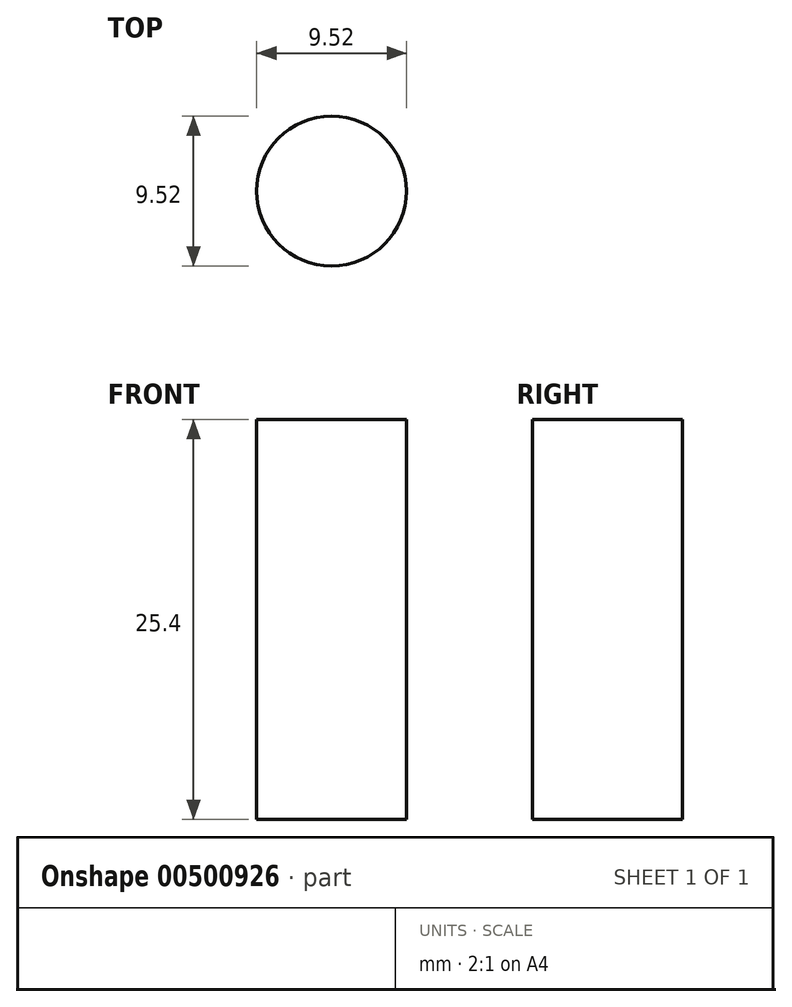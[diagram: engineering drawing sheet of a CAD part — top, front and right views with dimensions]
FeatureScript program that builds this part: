
annotation { "Feature Type Name" : "Feature", "Feature Type Description" : "" }
export const myFeature = defineFeature(function(context is Context, id is Id, definition is map)
    precondition{}
    {
        {
            var Q0;
            Q0=qCreatedBy(makeId("Top.planeOp"),FACE);
            var sketch = newSketch(context, id + "F0", { "sketchPlane" : qUnion([Q0])});
            skCircle(sketch, "E0", {"center": v(0, 0) * mm, "radius": 4.76 * mm});
            skSolve(sketch);
        }
        {
            var Q0;
            Q0=makeQuery(id+"F0.imprint","IMPRINT",FACE,{"disambiguationData":[TD([[makeQuery(id+"F0.imprint","IMPRINT",EDGE,{"derivedFrom":sQuery(id+"F0.wireOp",EDGE,"E0")}),1.0]])]});
            extrude(context, id + "F1", {"entities" : qUnion([Q0]), "endBound" : BoundingType.SYMMETRIC, "depth" : 25.4 * mm});
        }
    });
